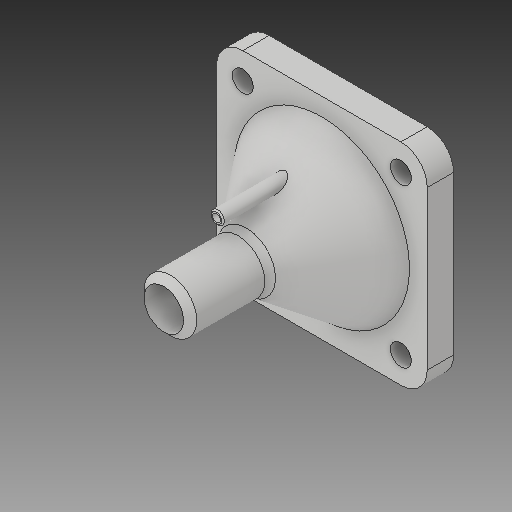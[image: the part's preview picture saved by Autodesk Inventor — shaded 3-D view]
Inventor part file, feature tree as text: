
AUTODESK INVENTOR PART (.ipt)
format: ipt  version: 2018 (Build 220112000, 112)  size: 365,056 bytes
history: native  units: in
note: dims shown in document units (in); Inventor stores cm internally (conversion verified against a paired STEP export)
features: extrude x12, sketch x10, fillet x4, projected_geometry x3, chamfer x2, hole x2, plane x1, loft x1, shell x1, pattern_circular x1
ambient origin geometry x8: Origin, YZ Plane, XZ Plane, XY Plane, X Axis, Y Axis, Z Axis, Center Point
bodies: Body1 (feature_tree)
feature tree (37):
  sketch  "Sketch26"  dims[d127=2.0in d128=4.0in d129=3.325in]
  plane  "Work Plane3"
  loft  "Loft2"
  shell  "Shell2"  Thickness=3.325in
  extrude  "Extrusion31"  Depth=1.0in
  fillet  "Fillet5"  [1 undecoded]
  extrude  "Extrusion32"  Depth=0.15in
  sketch  "Sketch31"  dims[d144=0.75in d145=0.5in d146=0.0in]
  extrude  "Extrusion33"  Depth=0.5in
  extrude  "Extrusion34"  Depth=0.5in TaperAngle=0.0deg
  extrude  "Extrusion35"  Depth=0.625in
  fillet  "Fillet6"  Radius=0.505in
  pattern_circular  "Circular Pattern4"  [2 undecoded]
  extrude  "Extrusion36"  Depth=0.5in TaperAngle=360.0deg
  fillet  "Fillet7"  Radius=1.5in
  chamfer  "Chamfer5"  Distance=0.25in
  sketch  "Sketch33"  dims[d150=0.25in]
  extrude  "Extrusion37"  Depth=0.125in TaperAngle=45.0deg
  extrude  "Extrusion38"  Depth=0.5in
  extrude  "Extrusion39"  Depth=0.25in
  chamfer  "Chamfer6"  Distance=0.05in
  extrude  "Extrusion40"  Depth=0.5in TaperAngle=0.0deg
  hole  "Hole2"  [1 undecoded]
  extrude  "Extrusion41"  Depth=0.5in TaperAngle=0.0deg
  extrude  "Extrusion42"  Depth=0.125in TaperAngle=45.0deg
  fillet  "Fillet8"  Radius=0.5in
  sketch  "Sketch27"  dims[d130=1.5in d131=1.0in d136=0.0in d137=90.0deg]
  sketch  "Sketch28"  dims[d138=0.0in d139=90.0deg d140=0.15in]
  projected_geometry  "Projected Loop14"
  sketch  "Sketch29"  dims[d141=0.5in d142=0.0in d143=1.0in]
  projected_geometry  "Projected Loop15"
  sketch  "Sketch32"  dims[d147=1.0in d148=0.625in d149=0.505in]
  sketch  "Sketch34"  dims[d151=0.5in d152=0.0in]
  hole  "Hole1"  [1 undecoded]
  sketch  "Sketch35"  dims[d153=0.5in d154=0.0in]
  sketch  "Sketch36"  dims[d155=0.2in d156=0.0in d157=0.25in d158=0.7874in d159=360.0deg d161=1.5in d162=0.0in d163=0.25in d164=0.125in d165=0.125in d166=45.0deg d167=1.0in d168=0.25in d169=0.05in d170=1.5in d171=0.0in d172=1.5in d173=0.0in d174=0.5in d175=0.0in d176=0.025in d177=0.125in d178=45.0deg d179=0.5in d180=0.0in d181=0.397in d182=0.75in d183=0.375in d184=0.25in d185=0.5635in d186=1.0in d187=0.0in d188=0.5in d189=0.0in d190=0.5in d191=0.0in d192=0.5in]
  projected_geometry  "Projected Loop16"
note: 5 required parameter values undecoded (feature->parameter linkage not recoverable at this tier; creation-order binding heuristic only, values carry confidence <= 0.55)
